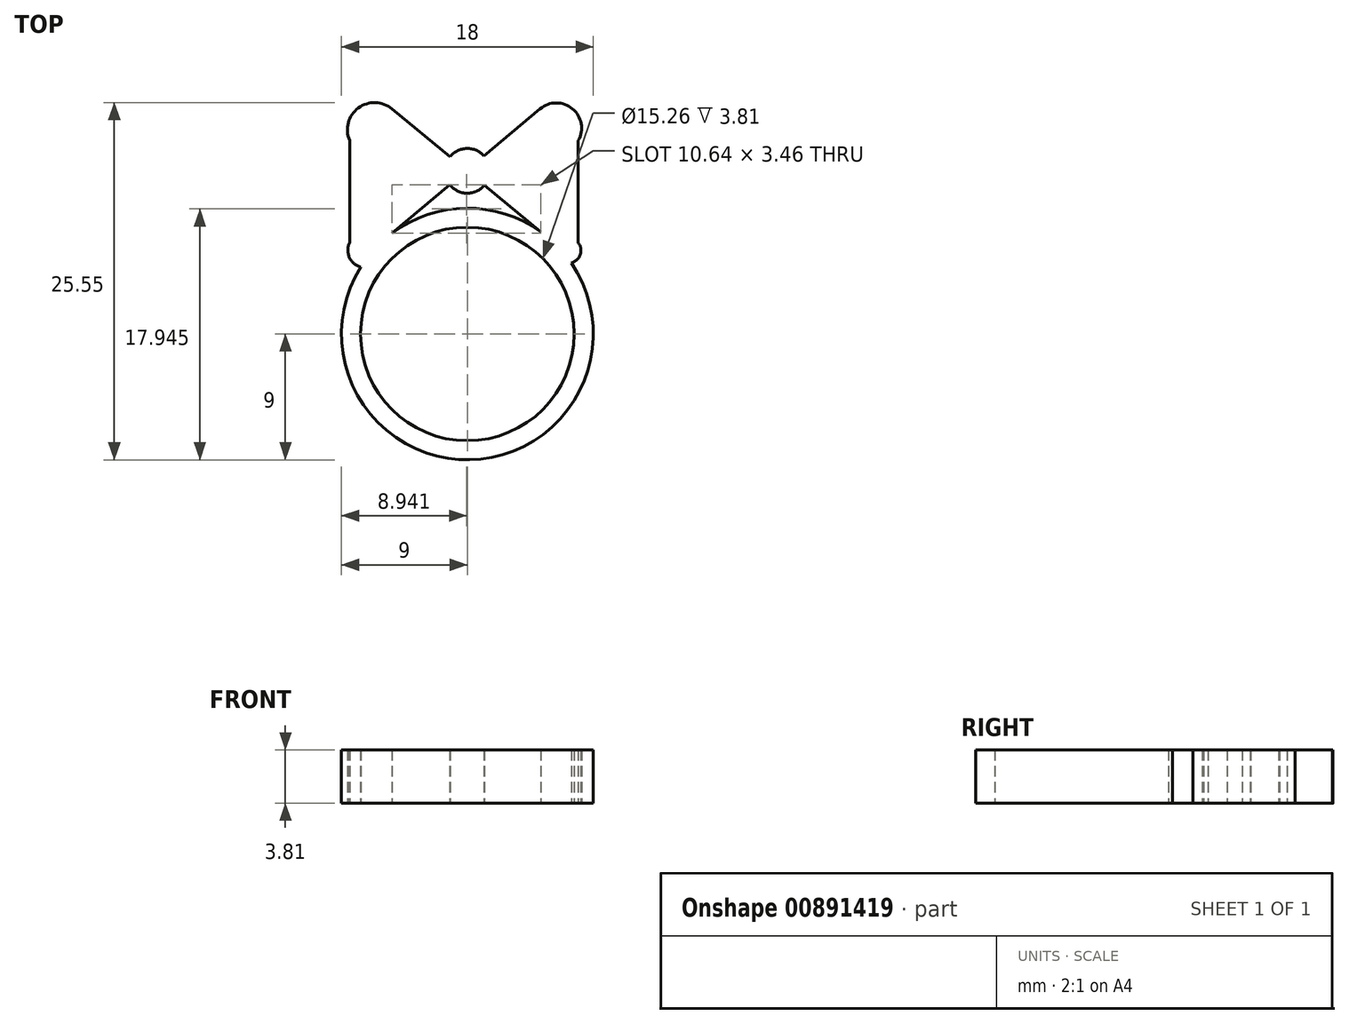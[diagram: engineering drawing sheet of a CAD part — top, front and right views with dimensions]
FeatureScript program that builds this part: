
annotation { "Feature Type Name" : "Feature", "Feature Type Description" : "" }
export const myFeature = defineFeature(function(context is Context, id is Id, definition is map)
    precondition{}
    {
        {
            var Q0;
            Q0=qCreatedBy(makeId("Top.planeOp"),FACE);
            var sketch = newSketch(context, id + "F0", { "sketchPlane" : qUnion([Q0])});
            skCircle(sketch, "E0", {"center": v(0, 0) * mm, "radius": 7.63 * mm});
            skArc(sketch, "E1", {"start": v(5.26, 7.3) * mm, "mid": v(-0.07, 9) * mm, "end": v(-5.38, 7.21) * mm});
            skArc(sketch, "E2", {"start": v(1.2, 12.73) * mm, "mid": v(-0.04, 13.27) * mm, "end": v(-1.24, 12.68) * mm});
            skLineSegment(sketch, "E3", {"start": v(5.26, 7.3) * mm, "end": v(1.23, 10.64) * mm});
            skPoint(sketch, "E4.start.orphan", {"position": v(-6.18, 6.54) * mm});
            skLineSegment(sketch, "E5", {"start": v(-5.38, 7.21) * mm, "end": v(-1.26, 10.68) * mm});
            skLineSegment(sketch, "E6", {"start": v(-8.41, 13.83) * mm, "end": v(-8.41, 6.54) * mm});
            skPoint(sketch, "E7.orphan", {"position": v(-13.52, 6.54) * mm});
            skPoint(sketch, "E8.orphan", {"position": v(-8.41, 17.53) * mm});
            skPoint(sketch, "E9.orphan", {"position": v(-7.1, 17.53) * mm});
            skPoint(sketch, "E10.orphan", {"position": v(7.92, 17.53) * mm});
            skArc(sketch, "E11", {"start": v(-5.39, 16.1) * mm, "mid": v(-7.8, 16.16) * mm, "end": v(-8.41, 13.83) * mm});
            skArc(sketch, "E12", {"start": v(7.92, 13.83) * mm, "mid": v(7.51, 16.1) * mm, "end": v(5.2, 16.1) * mm});
            skArc(sketch, "E13", {"start": v(-8.41, 6.54) * mm, "mid": v(-8.43, 5.47) * mm, "end": v(-7.62, 4.79) * mm});
            skArc(sketch, "E14", {"start": v(7.42, 5.08) * mm, "mid": v(8.06, 5.67) * mm, "end": v(7.92, 6.54) * mm});
            skPoint(sketch, "E15.orphan", {"position": v(6.36, 6.37) * mm});
            skArc(sketch, "E16.trimOffspring", {"start": v(-7.62, 4.79) * mm, "mid": v(0.18, -9) * mm, "end": v(7.42, 5.08) * mm});
            skLineSegment(sketch, "E17.trimOffspring", {"start": v(7.92, 13.83) * mm, "end": v(7.92, 6.54) * mm});
            skArc(sketch, "E18.trimOffspring", {"start": v(-1.26, 10.68) * mm, "mid": v(-0.03, 10.07) * mm, "end": v(1.23, 10.64) * mm});
            skLineSegment(sketch, "E19.trimOffspring", {"start": v(1.2, 12.73) * mm, "end": v(5.2, 16.1) * mm});
            skLineSegment(sketch, "E20.trimOffspring", {"start": v(-1.24, 12.68) * mm, "end": v(-5.39, 16.1) * mm});
            skPoint(sketch, "E21.orphan", {"position": v(6.18, 6.54) * mm});
            skSolve(sketch);
        }
        {
            var Q0;
            Q0 = qSketchRegion(id + "F0", true);
            extrude(context, id + "F1", {"entities" : qUnion([Q0]), "depth" : 3.8 * mm, "offsetDistance" : 25.4 * mm});
        }
    });
